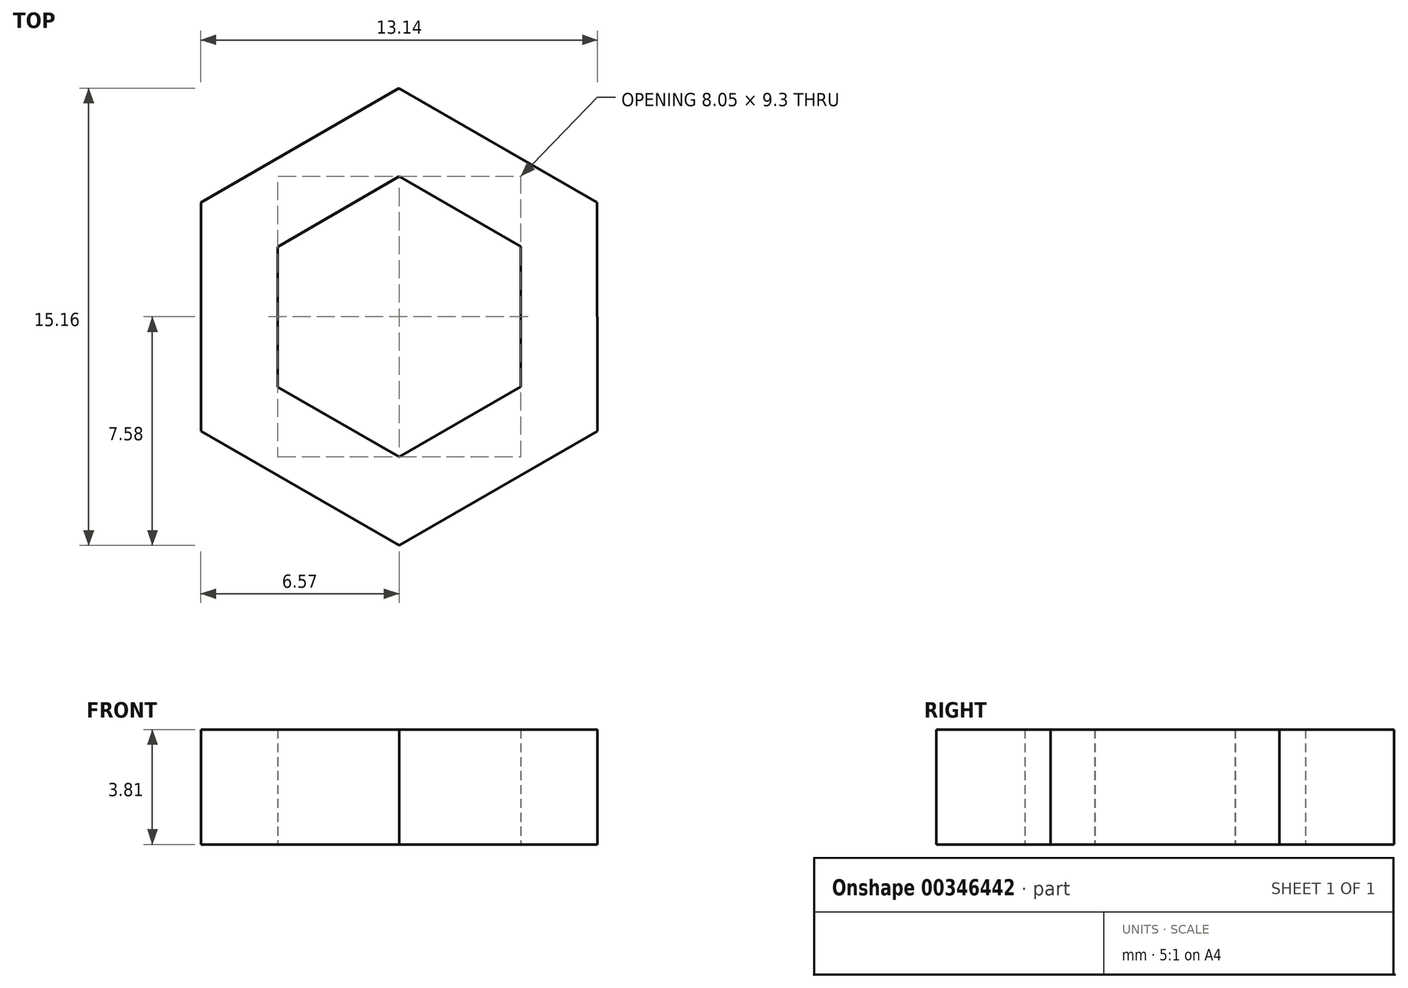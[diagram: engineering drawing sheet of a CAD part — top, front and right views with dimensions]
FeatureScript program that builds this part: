
annotation { "Feature Type Name" : "Feature", "Feature Type Description" : "" }
export const myFeature = defineFeature(function(context is Context, id is Id, definition is map)
    precondition{}
    {
        {
            var Q0;
            Q0=qCreatedBy(makeId("Top.planeOp"),FACE);
            var sketch = newSketch(context, id + "F0", { "sketchPlane" : qUnion([Q0])});
            skCircle(sketch, "E0.cCircle", {"center": v(0, 0) * mm, "radius": 4.03 * mm, "construction": true});
            skLineSegment(sketch, "E0.0", {"start": v(0, 4.65) * mm, "end": v(4.02, 2.33) * mm});
            skLineSegment(sketch, "E0.1", {"start": v(4.02, 2.33) * mm, "end": v(4.03, -2.32) * mm});
            skLineSegment(sketch, "E0.2", {"start": v(4.03, -2.32) * mm, "end": v(0, -4.65) * mm});
            skLineSegment(sketch, "E0.3", {"start": v(0, -4.65) * mm, "end": v(-4.02, -2.33) * mm});
            skLineSegment(sketch, "E0.4", {"start": v(-4.02, -2.33) * mm, "end": v(-4.03, 2.32) * mm});
            skLineSegment(sketch, "E0.5", {"start": v(-4.03, 2.32) * mm, "end": v(0, 4.65) * mm});
            skPoint(sketch, "E0.0.midPoint", {"position": v(2.01, 3.49) * mm});
            skCircle(sketch, "E1.cCircle", {"center": v(0, 0) * mm, "radius": 6.57 * mm, "construction": true});
            skLineSegment(sketch, "E1.0", {"start": v(0, 7.58) * mm, "end": v(6.56, 3.8) * mm});
            skLineSegment(sketch, "E1.1", {"start": v(6.56, 3.8) * mm, "end": v(6.57, -3.79) * mm});
            skLineSegment(sketch, "E1.2", {"start": v(6.57, -3.79) * mm, "end": v(0, -7.58) * mm});
            skLineSegment(sketch, "E1.3", {"start": v(0, -7.58) * mm, "end": v(-6.56, -3.8) * mm});
            skLineSegment(sketch, "E1.4", {"start": v(-6.56, -3.8) * mm, "end": v(-6.57, 3.79) * mm});
            skLineSegment(sketch, "E1.5", {"start": v(-6.57, 3.79) * mm, "end": v(0, 7.58) * mm});
            skPoint(sketch, "E1.0.midPoint", {"position": v(3.28, 5.69) * mm});
            skSolve(sketch);
        }
        {
            var Q0;
            Q0=qSketchRegion(id+"F0",true);
            extrude(context, id + "F1", {"entities" : qUnion([Q0]), "depth" : 3.8 * mm});
        }
    });
